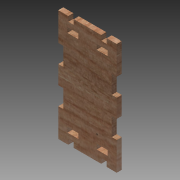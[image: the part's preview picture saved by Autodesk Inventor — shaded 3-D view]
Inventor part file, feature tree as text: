
AUTODESK INVENTOR PART (.ipt)
format: ipt  version: 2014 SP1 (Build 180222100, 222)  size: 326,144 bytes
history: native  units: mm
features: other x10, sketch x6, extrude x4
ambient origin geometry x8: Origin, YZ Plane, XZ Plane, XY Plane, X Axis, Y Axis, Z Axis, Center Point
bodies: Solid1 (feature_tree)
feature tree (20):
  other  "Blocks"
  extrude  "Extrusion1"  Depth=100.0mm
  extrude  "Extrusion3"  TaperAngle=0.0deg  [1 undecoded]
  extrude  "Extrusion4"  Depth=20.0mm
  extrude  "Extrusion7"  Depth=5.5mm
  sketch  "Sketch15"  dims[d16=0.0mm]
  sketch  "Sketch16"  dims[d17=5.5mm d18=12.0mm d19=20.0mm d20=5.5mm d21=0.0mm d22=11.0mm d23=6.0mm d24=5.5mm d32=15.0mm d33=5.5mm d34=0.0mm d55=64.0mm]
  other  "Kerf0.1"
  sketch  "Sketch1"  dims[d0=64.0mm d1=100.0mm]
  sketch  "Sketch5"  dims[d2=5.5mm d3=0.0mm]
  sketch  "Sketch6"  dims[d12=20.0mm d13=20.0mm]
  sketch  "Sketch7"  dims[d14=5.5mm d15=5.5mm]
  other  "Block1"
  other  "Block2"
  other  "Block3"
  other  "Block4"
  other  "Block3:1"
  other  "Block3:2"
  other  "Block4:1"
  other  "Block4:2"
note: 1 required parameter value undecoded (feature->parameter linkage not recoverable at this tier; creation-order binding heuristic only, values carry confidence <= 0.55)
